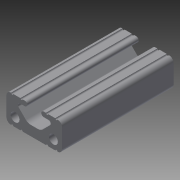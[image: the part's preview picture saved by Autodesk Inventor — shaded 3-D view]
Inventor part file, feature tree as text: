
AUTODESK INVENTOR PART (.ipt)
format: ipt  version: 2018 (Build 220112000, 112)  size: 135,680 bytes
history: native  units: in
note: dims shown in document units (in); Inventor stores cm internally (conversion verified against a paired STEP export)
features: extrude x1, sketch x1
ambient origin geometry x8: Origin, YZ Plane, XZ Plane, XY Plane, X Axis, Y Axis, Z Axis, Center Point
bodies: Solid1 (feature_tree)
feature tree (2):
  extrude  "Extrusion1"  [1 undecoded]
  sketch  "Sketch_1"  dims[d0=2.0in d1=0.0in]
note: 1 required parameter value undecoded (feature->parameter linkage not recoverable at this tier; creation-order binding heuristic only, values carry confidence <= 0.55)
